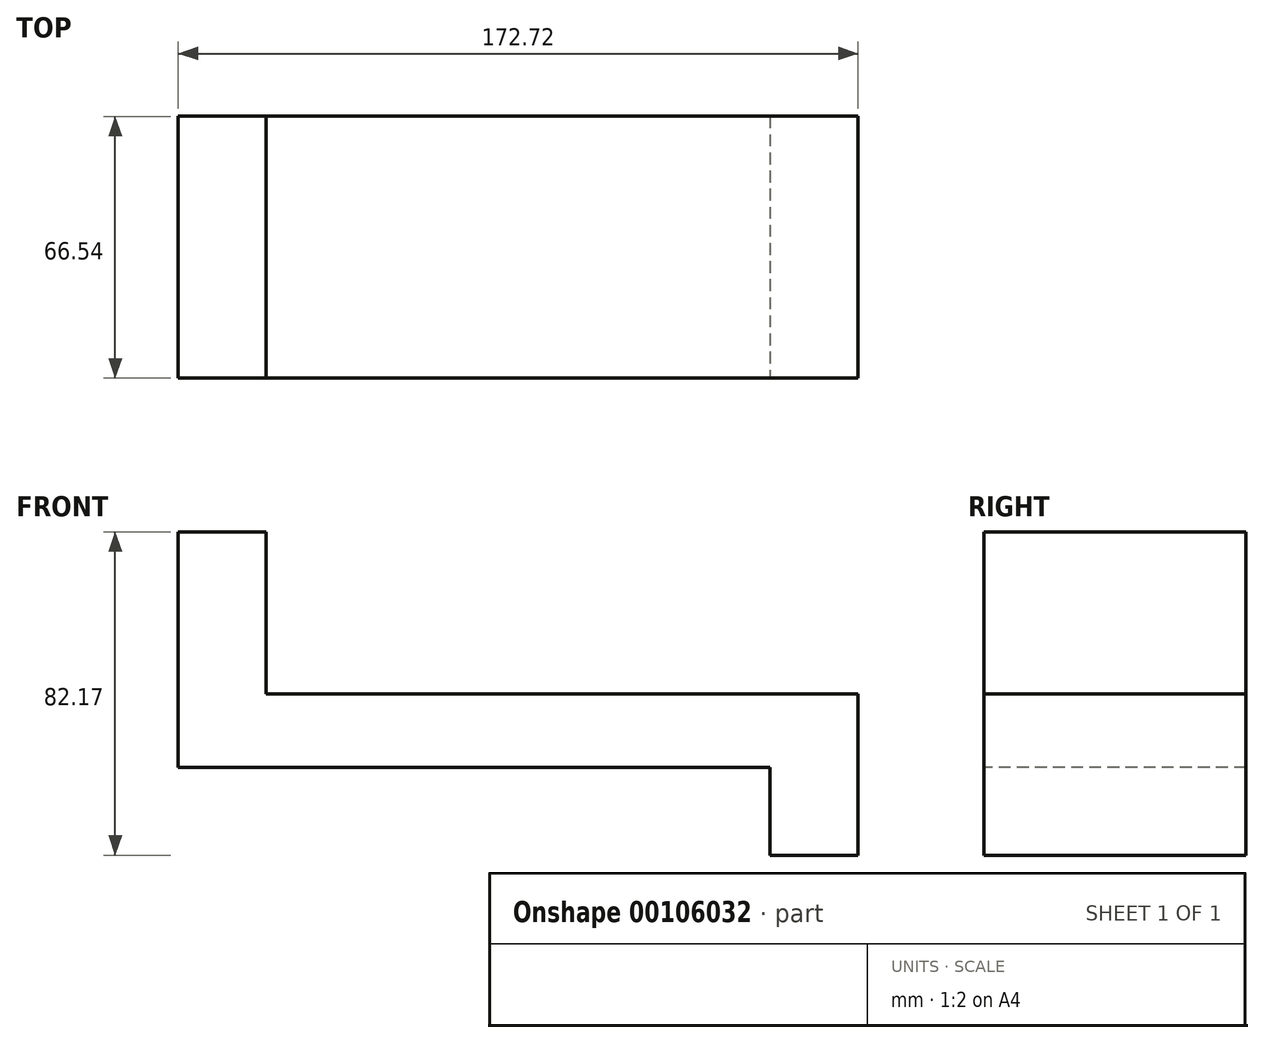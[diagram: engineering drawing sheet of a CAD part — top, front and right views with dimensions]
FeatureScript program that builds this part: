
annotation { "Feature Type Name" : "Feature", "Feature Type Description" : "" }
export const myFeature = defineFeature(function(context is Context, id is Id, definition is map)
    precondition{}
    {
        {
            var Q0;
            Q0=qCreatedBy(makeId("Top.planeOp"),FACE);
            var sketch = newSketch(context, id + "F0", { "sketchPlane" : qUnion([Q0])});
            skLineSegment(sketch, "E0.bottom", {"start": v(86.36, -33.27) * mm, "end": v(-86.36, -33.27) * mm});
            skLineSegment(sketch, "E0.top", {"start": v(86.36, 33.27) * mm, "end": v(-86.36, 33.27) * mm});
            skLineSegment(sketch, "E0.left", {"start": v(86.36, -33.27) * mm, "end": v(86.36, 33.27) * mm});
            skLineSegment(sketch, "E0.right", {"start": v(-86.36, -33.27) * mm, "end": v(-86.36, 33.27) * mm});
            skPoint(sketch, "E0.middle", {"position": v(0, 0) * mm});
            skSolve(sketch);
        }
        {
            var Q0;
            Q0=makeQuery(id+"F0.imprint","IMPRINT",FACE,{"disambiguationData":[TD([[makeQuery(id+"F0.imprint","IMPRINT",EDGE,{"derivedFrom":sQuery(id+"F0.wireOp",EDGE,"E0.bottom")}),-1.0]])]});
            extrude(context, id + "F1", {"entities" : qUnion([Q0]), "depth" : 63.5 * mm});
        }
        {
            var Q0;
            Q0=makeQuery(id+"F1.opExtrude","SWEPT_FACE",FACE,{"disambiguationData":[OSD([sQuery(id+"F0.wireOp",EDGE,"E0.bottom")])]});
            var sketch = newSketch(context, id + "F2", { "sketchPlane" : qUnion([Q0])});
            skLineSegment(sketch, "E1", {"start": v(86.36, 0) * mm, "end": v(64, 0) * mm});
            skLineSegment(sketch, "E2", {"start": v(64, 0) * mm, "end": v(64, 22.35) * mm});
            skLineSegment(sketch, "E3", {"start": v(64, 22.35) * mm, "end": v(-86.36, 22.35) * mm});
            skSolve(sketch);
        }
        {
            var Q0;
            {var subQ0=sQuery(id+"F2.wireOp",EDGE,"E2");Q0=makeQuery(id+"F2.imprint","IMPRINT",FACE,{"disambiguationData":[TD([[makeQuery(id+"F2.imprint","IMPRINT",EDGE,{"derivedFrom":subQ0}),1.0]])]});}
            extrude(context, id + "F3", {"entities" : qUnion([Q0]), "operationType" : NewBodyOperationType.REMOVE, "oppositeDirection" : true, "depth" : 189.63 * mm});
        }
        {
            var Q0;
            Q0=makeQuery(id+"F1.opExtrude","CAP_FACE",FACE,{"disambiguationData":[OSD([sQuery(id+"F0.wireOp",EDGE,"E0.bottom"),sQuery(id+"F0.wireOp",EDGE,"E0.top"),sQuery(id+"F0.wireOp",EDGE,"E0.left"),sQuery(id+"F0.wireOp",EDGE,"E0.right")])],"isStart":false});
            var sketch = newSketch(context, id + "F4", { "sketchPlane" : qUnion([Q0])});
            skLineSegment(sketch, "E4", {"start": v(-86.36, -33.27) * mm, "end": v(-64, -33.27) * mm});
            skLineSegment(sketch, "E5", {"start": v(-64, -33.27) * mm, "end": v(-64, 33.27) * mm});
            skLineSegment(sketch, "E6", {"start": v(-64, 33.27) * mm, "end": v(-86.36, 33.27) * mm});
            skLineSegment(sketch, "E7", {"start": v(-86.36, 33.27) * mm, "end": v(-86.36, -33.27) * mm});
            skSolve(sketch);
        }
        {
            var Q0;
            {var subQ0=sQuery(id+"F4.wireOp",EDGE,"E5");Q0=makeQuery(id+"F4.imprint","IMPRINT",FACE,{"disambiguationData":[TD([[makeQuery(id+"F4.imprint","IMPRINT",EDGE,{"derivedFrom":subQ0}),-1.0]])]});}
            extrude(context, id + "F5", {"entities" : qUnion([Q0]), "operationType" : NewBodyOperationType.REMOVE, "oppositeDirection" : true, "depth" : 22.54 * mm});
        }
        {
            var Q0;
            Q0=makeQuery(id+"F1.opExtrude","CAP_FACE",FACE,{"disambiguationData":[OSD([sQuery(id+"F0.wireOp",EDGE,"E0.bottom"),sQuery(id+"F0.wireOp",EDGE,"E0.top"),sQuery(id+"F0.wireOp",EDGE,"E0.left"),sQuery(id+"F0.wireOp",EDGE,"E0.right")])],"isStart":false});
            extrude(context, id + "F6", {"entities" : qUnion([Q0]), "operationType" : NewBodyOperationType.ADD, "depth" : 63.5 * mm});
        }
        {
            var Q0;
            Q0=makeQuery(id+"F6.opExtrude","CAP_FACE",FACE,{"disambiguationData":[OSD([sQuery(id+"F0.wireOp",EDGE,"E0.bottom"),sQuery(id+"F0.wireOp",EDGE,"E0.top"),sQuery(id+"F0.wireOp",EDGE,"E0.left"),sQuery(id+"F0.wireOp",EDGE,"E0.right")])],"isStart":false});
            extrude(context, id + "F7", {"entities" : qUnion([Q0]), "operationType" : NewBodyOperationType.REMOVE, "oppositeDirection" : true, "depth" : 41.46 * mm});
        }
        {
            var Q0;
            Q0=makeQuery(id+"F7.boolean.opBoolean","COPY",FACE,{"derivedFrom":makeQuery(id+"F7.opExtrude","CAP_FACE",FACE,{"disambiguationData":[OSD([sQuery(id+"F0.wireOp",EDGE,"E0.bottom"),sQuery(id+"F0.wireOp",EDGE,"E0.top"),sQuery(id+"F0.wireOp",EDGE,"E0.left"),sQuery(id+"F0.wireOp",EDGE,"E0.right")])],"isStart":false})});
            extrude(context, id + "F8", {"entities" : qUnion([Q0]), "operationType" : NewBodyOperationType.REMOVE, "oppositeDirection" : true, "depth" : 3.37 * mm});
        }
    });
